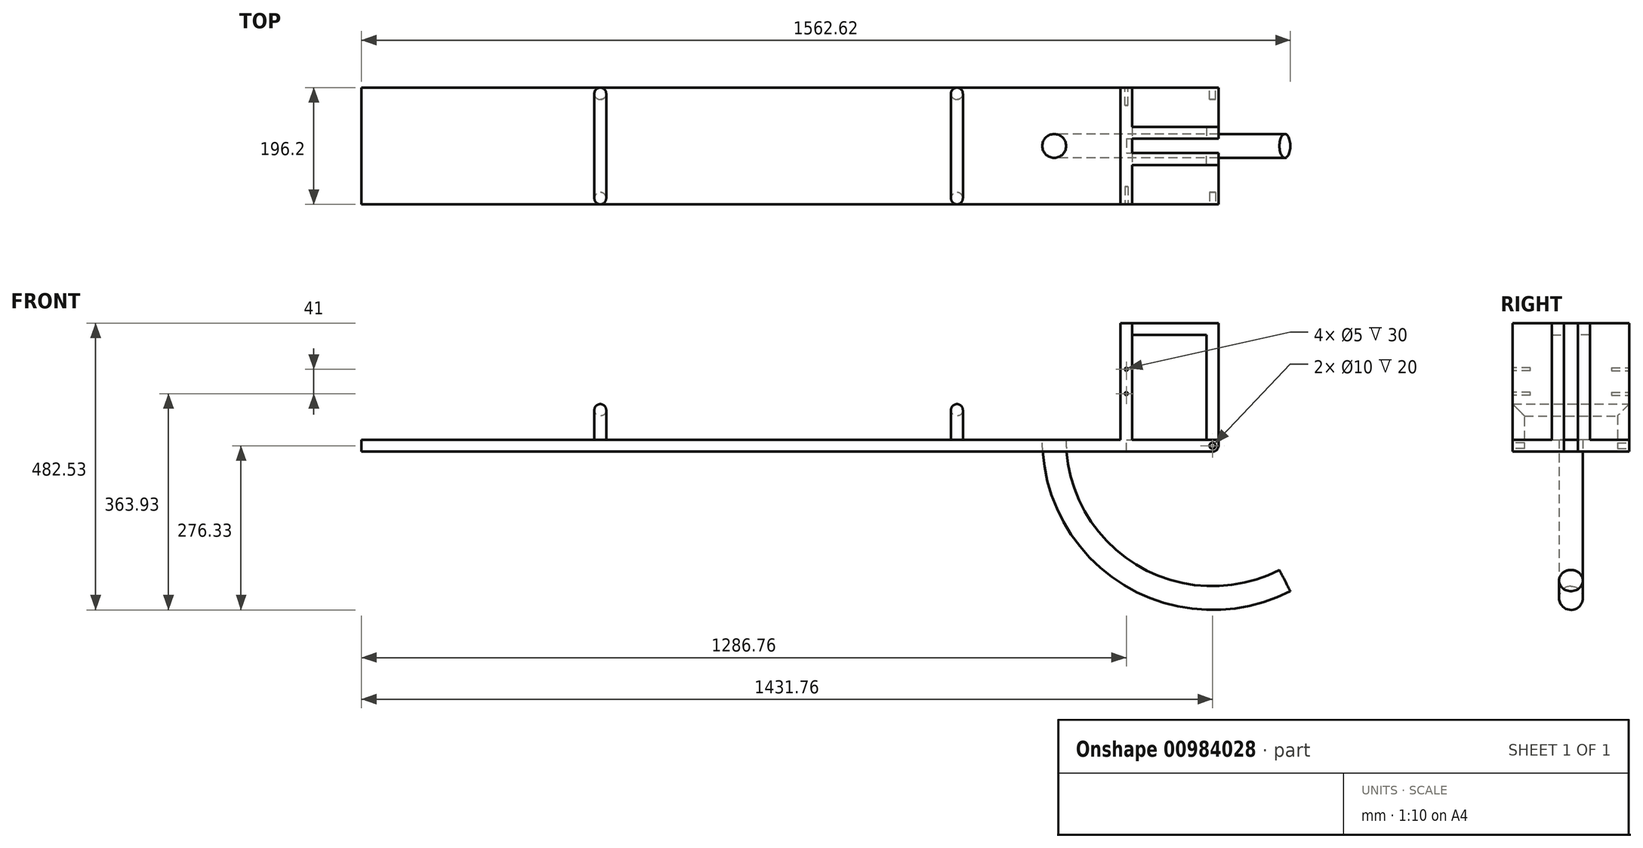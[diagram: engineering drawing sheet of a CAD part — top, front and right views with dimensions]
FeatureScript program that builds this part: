
annotation { "Feature Type Name" : "Feature", "Feature Type Description" : "" }
export const myFeature = defineFeature(function(context is Context, id is Id, definition is map)
    precondition{}
    {
        {
            var Q0;
            Q0=qCreatedBy(makeId("Top.planeOp"),FACE);
            var sketch = newSketch(context, id + "F0", { "sketchPlane" : qUnion([Q0])});
            skLineSegment(sketch, "E0", {"start": v(0, -12) * mm, "end": v(0, -98.1) * mm});
            skLineSegment(sketch, "E1", {"start": v(0, -98.1) * mm, "end": v(-1441.76, -98.1) * mm});
            skLineSegment(sketch, "E2", {"start": v(-1441.76, -98.1) * mm, "end": v(-1441.76, 98.1) * mm});
            skLineSegment(sketch, "E3", {"start": v(-1441.76, 98.1) * mm, "end": v(0, 98.1) * mm});
            skLineSegment(sketch, "E4", {"start": v(0, 98.1) * mm, "end": v(0, 12) * mm});
            skLineSegment(sketch, "E5", {"start": v(-155, 0) * mm, "end": v(-155, -12) * mm});
            skLineSegment(sketch, "E6.MirrorCS", {"start": v(-155, 0) * mm, "end": v(-155, 12) * mm});
            skLineSegment(sketch, "E7", {"start": v(-155, 12) * mm, "end": v(0, 12) * mm});
            skLineSegment(sketch, "E8", {"start": v(-155, -12) * mm, "end": v(0, -12) * mm});
            skSolve(sketch);
        }
        {
            var Q0;
            Q0=makeQuery(id+"F0.imprint","IMPRINT",FACE,{"disambiguationData":[TD([[makeQuery(id+"F0.imprint","IMPRINT",EDGE,{"derivedFrom":sQuery(id+"F0.wireOp",EDGE,"E0")}),-1.0]])]});
            extrude(context, id + "F1", {"entities" : qUnion([Q0]), "oppositeDirection" : true, "depth" : 20 * mm, "offsetDistance" : 25 * mm});
        }
        {
            var Q0;
            Q0=makeQuery(id+"F1.opExtrude","CAP_EDGE",EDGE,{"disambiguationData":[OSD([sQuery(id+"F0.wireOp",EDGE,"E0")])],"isStart":false});
            var Q1;
            Q1=makeQuery(id+"F1.opExtrude","CAP_EDGE",EDGE,{"disambiguationData":[OSD([sQuery(id+"F0.wireOp",EDGE,"E4")])],"isStart":false});
            fillet(context, id + "F2", {"entities" : qUnion([Q0, Q1]), "radius" : 10 * mm, "tangentPropagation" : true, "allowEdgeOverflow" : false});
        }
        {
            var Q0;
            Q0=qCreatedBy(makeId("Top.planeOp"),FACE);
            var sketch = newSketch(context, id + "F3", { "sketchPlane" : qUnion([Q0])});
            skLineSegment(sketch, "E9", {"start": v(-440, -98.1) * mm, "end": v(-440, -88.1) * mm});
            skLineSegment(sketch, "E10", {"start": v(-1040, -98.1) * mm, "end": v(-1040, -88.1) * mm});
            skCircle(sketch, "E11", {"center": v(-440, -88.1) * mm, "radius": 10 * mm});
            skCircle(sketch, "E12", {"center": v(-1040, -88.1) * mm, "radius": 10 * mm});
            skSolve(sketch);
        }
        {
            var Q0;
            Q0=qCreatedBy(makeId("Front.planeOp"),FACE);
            var sketch = newSketch(context, id + "F4", { "sketchPlane" : qUnion([Q0])});
            skLineSegment(sketch, "E13", {"start": v(0, 0) * mm, "end": v(-10, 0) * mm});
            skArc(sketch, "E14", {"start": v(-276.33, 0) * mm, "mid": v(-148.77, -227.32) * mm, "end": v(111.72, -236.89) * mm});
            skLineSegment(sketch, "E15", {"start": v(-10, 0) * mm, "end": v(-276.33, 0) * mm});
            skSolve(sketch);
        }
        {
            var Q0;
            Q0=qCreatedBy(makeId("Top.planeOp"),FACE);
            var sketch = newSketch(context, id + "F5", { "sketchPlane" : qUnion([Q0])});
            skLineSegment(sketch, "E16", {"start": v(0, 0) * mm, "end": v(-239.12, 0) * mm});
            skLineSegment(sketch, "E17", {"start": v(0, 0) * mm, "end": v(-276.33, 0) * mm});
            skCircle(sketch, "E18", {"center": v(-276.33, 0) * mm, "radius": 20 * mm});
            skSolve(sketch);
        }
        {
            var Q0;
            Q0=makeQuery(id+"F5.imprint","IMPRINT",FACE,{"disambiguationData":[TD([[makeQuery(id+"F5.imprint","IMPRINT",EDGE,{"derivedFrom":sQuery(id+"F5.wireOp",EDGE,"E18")}),1.0]])]});
            var Q1;
            Q1=sQuery(id+"F4.wireOp",EDGE,"E14");
            sweep(context, id + "F6", {"profiles" : qUnion([Q0]), "path" : qUnion([Q1])});
        }
        {
            var Q0;
            Q0=makeQuery(id+"F1.opExtrude","SWEPT_FACE",FACE,{"disambiguationData":[OSD([sQuery(id+"F0.wireOp",EDGE,"E1")])]});
            cPlane(context, id + "F7", {"entities" : qUnion([Q0]), "cplaneType" : CPlaneType.OFFSET, "offset" : 0 * mm, "width" : 150 * mm, "height" : 150 * mm});
        }
        {
            var Q0;
            Q0=qCreatedBy(id+"F7.planeOp",FACE);
            var sketch = newSketch(context, id + "F8", { "sketchPlane" : qUnion([Q0])});
            skLineSegment(sketch, "E19", {"start": v(-145, 0) * mm, "end": v(-155, 0) * mm});
            skLineSegment(sketch, "E20", {"start": v(-155, 196.2) * mm, "end": v(-145, 196.2) * mm});
            skLineSegment(sketch, "E21", {"start": v(-155, 196.2) * mm, "end": v(-165, 196.2) * mm});
            skLineSegment(sketch, "E22", {"start": v(-145, 196.2) * mm, "end": v(-145, 0) * mm});
            skLineSegment(sketch, "E23", {"start": v(-165, 196.2) * mm, "end": v(-165, 0) * mm});
            skLineSegment(sketch, "E24", {"start": v(-155, 0) * mm, "end": v(-165, 0) * mm});
            skSolve(sketch);
        }
        {
            var Q0;
            Q0=makeQuery(id+"F8.imprint","IMPRINT",FACE,{"disambiguationData":[TD([[makeQuery(id+"F8.imprint","IMPRINT",EDGE,{"derivedFrom":sQuery(id+"F8.wireOp",EDGE,"E19")}),-1.0]])]});
            extrude(context, id + "F9", {"entities" : qUnion([Q0]), "oppositeDirection" : true, "depth" : 196.2 * mm, "offsetDistance" : 25 * mm});
        }
        {
            var Q0;
            Q0=makeQuery(id+"F9.opExtrude","CAP_FACE",FACE,{"disambiguationData":[OSD([sQuery(id+"F8.wireOp",EDGE,"E19"),sQuery(id+"F8.wireOp",EDGE,"E20"),sQuery(id+"F8.wireOp",EDGE,"E21"),sQuery(id+"F8.wireOp",EDGE,"E22"),sQuery(id+"F8.wireOp",EDGE,"E23"),sQuery(id+"F8.wireOp",EDGE,"E24")])],"isStart":true});
            cPlane(context, id + "F10", {"entities" : qUnion([Q0]), "cplaneType" : CPlaneType.OFFSET, "offset" : 0 * mm, "width" : 150 * mm, "height" : 150 * mm});
        }
        {
            var Q0;
            Q0=qCreatedBy(id+"F10.planeOp",FACE);
            var sketch = newSketch(context, id + "F11", { "sketchPlane" : qUnion([Q0])});
            skLineSegment(sketch, "E25", {"start": v(0, 0) * mm, "end": v(-155, 0) * mm});
            skCircle(sketch, "E26", {"center": v(-155, 77.6) * mm, "radius": 2.5 * mm});
            skCircle(sketch, "E27", {"center": v(-155, 118.6) * mm, "radius": 2.5 * mm});
            skSolve(sketch);
        }
        {
            var Q0;
            Q0=makeQuery(id+"F11.imprint","IMPRINT",FACE,{"disambiguationData":[TD([[makeQuery(id+"F11.imprint","IMPRINT",EDGE,{"derivedFrom":sQuery(id+"F11.wireOp",EDGE,"E27")}),1.0]])]});
            var Q1;
            Q1=makeQuery(id+"F11.imprint","IMPRINT",FACE,{"disambiguationData":[TD([[makeQuery(id+"F11.imprint","IMPRINT",EDGE,{"derivedFrom":sQuery(id+"F11.wireOp",EDGE,"E26")}),1.0]])]});
            extrude(context, id + "F12", {"entities" : qUnion([Q0, Q1]), "operationType" : NewBodyOperationType.REMOVE, "oppositeDirection" : true, "depth" : 30 * mm, "offsetDistance" : 25 * mm});
        }
        {
            var Q0;
            Q0=makeQuery(id+"F9.opExtrude","CAP_FACE",FACE,{"disambiguationData":[OSD([sQuery(id+"F8.wireOp",EDGE,"E19"),sQuery(id+"F8.wireOp",EDGE,"E20"),sQuery(id+"F8.wireOp",EDGE,"E21"),sQuery(id+"F8.wireOp",EDGE,"E22"),sQuery(id+"F8.wireOp",EDGE,"E23"),sQuery(id+"F8.wireOp",EDGE,"E24")])],"isStart":false});
            cPlane(context, id + "F13", {"entities" : qUnion([Q0]), "cplaneType" : CPlaneType.OFFSET, "offset" : 0 * mm, "width" : 150 * mm, "height" : 150 * mm});
        }
        {
            var Q0;
            Q0=qCreatedBy(id+"F13.planeOp",FACE);
            var sketch = newSketch(context, id + "F14", { "sketchPlane" : qUnion([Q0])});
            skLineSegment(sketch, "E28", {"start": v(0, 0) * mm, "end": v(155, 0) * mm});
            skCircle(sketch, "E29", {"center": v(155, 77.6) * mm, "radius": 2.5 * mm});
            skCircle(sketch, "E30", {"center": v(155, 118.6) * mm, "radius": 2.5 * mm});
            skSolve(sketch);
        }
        {
            var Q0;
            Q0=makeQuery(id+"F14.imprint","IMPRINT",FACE,{"disambiguationData":[TD([[makeQuery(id+"F14.imprint","IMPRINT",EDGE,{"derivedFrom":sQuery(id+"F14.wireOp",EDGE,"E30")}),1.0]])]});
            var Q1;
            Q1=makeQuery(id+"F14.imprint","IMPRINT",FACE,{"disambiguationData":[TD([[makeQuery(id+"F14.imprint","IMPRINT",EDGE,{"derivedFrom":sQuery(id+"F14.wireOp",EDGE,"E29")}),1.0]])]});
            extrude(context, id + "F15", {"entities" : qUnion([Q0, Q1]), "operationType" : NewBodyOperationType.REMOVE, "oppositeDirection" : true, "depth" : 30 * mm, "offsetDistance" : 25 * mm});
        }
        {
            var Q0;
            Q0=makeQuery(id+"F1.opExtrude","SWEPT_FACE",FACE,{"disambiguationData":[OSD([sQuery(id+"F0.wireOp",EDGE,"E7")])]});
            cPlane(context, id + "F16", {"entities" : qUnion([Q0]), "cplaneType" : CPlaneType.OFFSET, "offset" : 0 * mm, "width" : 150 * mm, "height" : 150 * mm});
        }
        {
            var Q0;
            Q0=qCreatedBy(id+"F16.planeOp",FACE);
            var sketch = newSketch(context, id + "F17", { "sketchPlane" : qUnion([Q0])});
            skLineSegment(sketch, "E31", {"start": v(0, 0) * mm, "end": v(0, 196.2) * mm});
            skLineSegment(sketch, "E32", {"start": v(0, 196.2) * mm, "end": v(-145, 196.2) * mm});
            skLineSegment(sketch, "E33", {"start": v(0, 0) * mm, "end": v(-20, 0) * mm});
            skLineSegment(sketch, "E34", {"start": v(-20, 0) * mm, "end": v(-20, 176.2) * mm});
            skLineSegment(sketch, "E35", {"start": v(-20, 176.2) * mm, "end": v(-145, 176.2) * mm});
            skLineSegment(sketch, "E36", {"start": v(-145, 196.2) * mm, "end": v(-145, 176.2) * mm});
            skSolve(sketch);
        }
        {
            var Q0;
            Q0=makeQuery(id+"F17.imprint","IMPRINT",FACE,{"disambiguationData":[TD([[makeQuery(id+"F17.imprint","IMPRINT",EDGE,{"derivedFrom":sQuery(id+"F17.wireOp",EDGE,"E31")}),1.0]])]});
            extrude(context, id + "F18", {"entities" : qUnion([Q0]), "operationType" : NewBodyOperationType.ADD, "oppositeDirection" : true, "depth" : 20 * mm, "offsetDistance" : 25 * mm});
        }
        {
            var Q0;
            Q0=makeQuery(id+"F1.opExtrude","SWEPT_FACE",FACE,{"disambiguationData":[OSD([sQuery(id+"F0.wireOp",EDGE,"E8")])]});
            cPlane(context, id + "F19", {"entities" : qUnion([Q0]), "cplaneType" : CPlaneType.OFFSET, "offset" : 0 * mm, "width" : 150 * mm, "height" : 150 * mm});
        }
        {
            var Q0;
            Q0=qCreatedBy(id+"F19.planeOp",FACE);
            var sketch = newSketch(context, id + "F20", { "sketchPlane" : qUnion([Q0])});
            skLineSegment(sketch, "E37", {"start": v(0, 0) * mm, "end": v(0, 196.2) * mm});
            skLineSegment(sketch, "E38", {"start": v(0, 196.2) * mm, "end": v(145, 196.2) * mm});
            skLineSegment(sketch, "E39", {"start": v(145, 196.2) * mm, "end": v(145, 176.2) * mm});
            skLineSegment(sketch, "E40", {"start": v(0, 0) * mm, "end": v(20, 0) * mm});
            skLineSegment(sketch, "E41", {"start": v(20, 0) * mm, "end": v(20, 176.2) * mm});
            skLineSegment(sketch, "E42", {"start": v(145, 176.2) * mm, "end": v(20, 176.2) * mm});
            skSolve(sketch);
        }
        {
            var Q0;
            Q0=makeQuery(id+"F20.imprint","IMPRINT",FACE,{"disambiguationData":[TD([[makeQuery(id+"F20.imprint","IMPRINT",EDGE,{"derivedFrom":sQuery(id+"F20.wireOp",EDGE,"E37")}),-1.0]])]});
            extrude(context, id + "F21", {"entities" : qUnion([Q0]), "operationType" : NewBodyOperationType.ADD, "oppositeDirection" : true, "depth" : 20 * mm, "offsetDistance" : 25 * mm});
        }
        {
            var Q0;
            Q0=qCreatedBy(id+"F7.planeOp",FACE);
            var sketch = newSketch(context, id + "F22", { "sketchPlane" : qUnion([Q0])});
            skLineSegment(sketch, "E43", {"start": v(0, 0) * mm, "end": v(-10, 0) * mm});
            skLineSegment(sketch, "E44", {"start": v(-10, 0) * mm, "end": v(-10, -10) * mm});
            skCircle(sketch, "E45", {"center": v(-10, -10) * mm, "radius": 5 * mm});
            skSolve(sketch);
        }
        {
            var Q0;
            Q0=makeQuery(id+"F22.imprint","IMPRINT",FACE,{"disambiguationData":[TD([[makeQuery(id+"F22.imprint","IMPRINT",EDGE,{"derivedFrom":sQuery(id+"F22.wireOp",EDGE,"E45")}),1.0]])]});
            extrude(context, id + "F23", {"entities" : qUnion([Q0]), "operationType" : NewBodyOperationType.REMOVE, "oppositeDirection" : true, "depth" : 20 * mm, "offsetDistance" : 25 * mm});
        }
        {
            var Q0;
            Q0=makeQuery(id+"F1.opExtrude","SWEPT_FACE",FACE,{"disambiguationData":[OSD([sQuery(id+"F0.wireOp",EDGE,"E3")])]});
            cPlane(context, id + "F24", {"entities" : qUnion([Q0]), "cplaneType" : CPlaneType.OFFSET, "offset" : 0 * mm, "width" : 150 * mm, "height" : 150 * mm});
        }
        {
            var Q0;
            Q0=qCreatedBy(id+"F24.planeOp",FACE);
            var sketch = newSketch(context, id + "F25", { "sketchPlane" : qUnion([Q0])});
            skLineSegment(sketch, "E46", {"start": v(0, 0) * mm, "end": v(10, 0) * mm});
            skLineSegment(sketch, "E47", {"start": v(10, 0) * mm, "end": v(10, -10) * mm});
            skCircle(sketch, "E48", {"center": v(10, -10) * mm, "radius": 5 * mm});
            skSolve(sketch);
        }
        {
            var Q0;
            Q0=makeQuery(id+"F25.imprint","IMPRINT",FACE,{"disambiguationData":[TD([[makeQuery(id+"F25.imprint","IMPRINT",EDGE,{"derivedFrom":sQuery(id+"F25.wireOp",EDGE,"E48")}),1.0]])]});
            extrude(context, id + "F26", {"entities" : qUnion([Q0]), "operationType" : NewBodyOperationType.REMOVE, "oppositeDirection" : true, "depth" : 20 * mm, "offsetDistance" : 25 * mm});
        }
        {
            var Q0;
            Q0=makeQuery(id+"F1.opExtrude","SWEPT_FACE",FACE,{"disambiguationData":[OSD([sQuery(id+"F0.wireOp",EDGE,"E2")])]});
            cPlane(context, id + "F27", {"entities" : qUnion([Q0]), "cplaneType" : CPlaneType.OFFSET, "offset" : 1001.76 * mm, "oppositeDirection" : true, "width" : 150 * mm, "height" : 150 * mm});
        }
        {
            var Q0;
            Q0=qCreatedBy(id+"F27.planeOp",FACE);
            var sketch = newSketch(context, id + "F28", { "sketchPlane" : qUnion([Q0])});
            skLineSegment(sketch, "E49", {"start": v(88.1, 0) * mm, "end": v(88.1, 50) * mm});
            skLineSegment(sketch, "E50", {"start": v(88.1, 50) * mm, "end": v(-88.1, 50) * mm});
            skLineSegment(sketch, "E51", {"start": v(-88.1, 50) * mm, "end": v(-88.1, 0) * mm});
            skSolve(sketch);
        }
        {
            var Q0;
            Q0=makeQuery(id+"F3.imprint","IMPRINT",FACE,{"disambiguationData":[TD([[makeQuery(id+"F3.imprint","IMPRINT",EDGE,{"derivedFrom":sQuery(id+"F3.wireOp",EDGE,"E11")}),1.0]])]});
            var Q1;
            Q1=sQuery(id+"F28.wireOp",EDGE,"E49");
            var Q2;
            Q2=sQuery(id+"F28.wireOp",EDGE,"E50");
            var Q3;
            Q3=sQuery(id+"F28.wireOp",EDGE,"E51");
            sweep(context, id + "F29", {"profiles" : qUnion([Q0]), "path" : qUnion([Q1, Q2, Q3])});
        }
        {
            var Q0;
            Q0=makeQuery(id+"F1.opExtrude","SWEPT_FACE",FACE,{"disambiguationData":[OSD([sQuery(id+"F0.wireOp",EDGE,"E2")])]});
            cPlane(context, id + "F30", {"entities" : qUnion([Q0]), "cplaneType" : CPlaneType.OFFSET, "offset" : 401.76 * mm, "oppositeDirection" : true, "width" : 150 * mm, "height" : 150 * mm});
        }
        {
            var Q0;
            Q0=qCreatedBy(id+"F30.planeOp",FACE);
            var sketch = newSketch(context, id + "F31", { "sketchPlane" : qUnion([Q0])});
            skLineSegment(sketch, "E52", {"start": v(0, 0) * mm, "end": v(88.1, 0) * mm});
            skLineSegment(sketch, "E53", {"start": v(88.1, 0) * mm, "end": v(88.1, 50) * mm});
            skLineSegment(sketch, "E54", {"start": v(88.1, 50) * mm, "end": v(-88.1, 50) * mm});
            skLineSegment(sketch, "E55", {"start": v(-88.1, 50) * mm, "end": v(-88.1, 0) * mm});
            skSolve(sketch);
        }
        {
            var Q0;
            Q0=makeQuery(id+"F3.imprint","IMPRINT",FACE,{"disambiguationData":[TD([[makeQuery(id+"F3.imprint","IMPRINT",EDGE,{"derivedFrom":sQuery(id+"F3.wireOp",EDGE,"E12")}),1.0]])]});
            var Q1;
            Q1=sQuery(id+"F31.wireOp",EDGE,"E53");
            var Q2;
            Q2=sQuery(id+"F31.wireOp",EDGE,"E54");
            var Q3;
            Q3=sQuery(id+"F31.wireOp",EDGE,"E55");
            sweep(context, id + "F32", {"profiles" : qUnion([Q0]), "path" : qUnion([Q1, Q2, Q3])});
        }
    });
